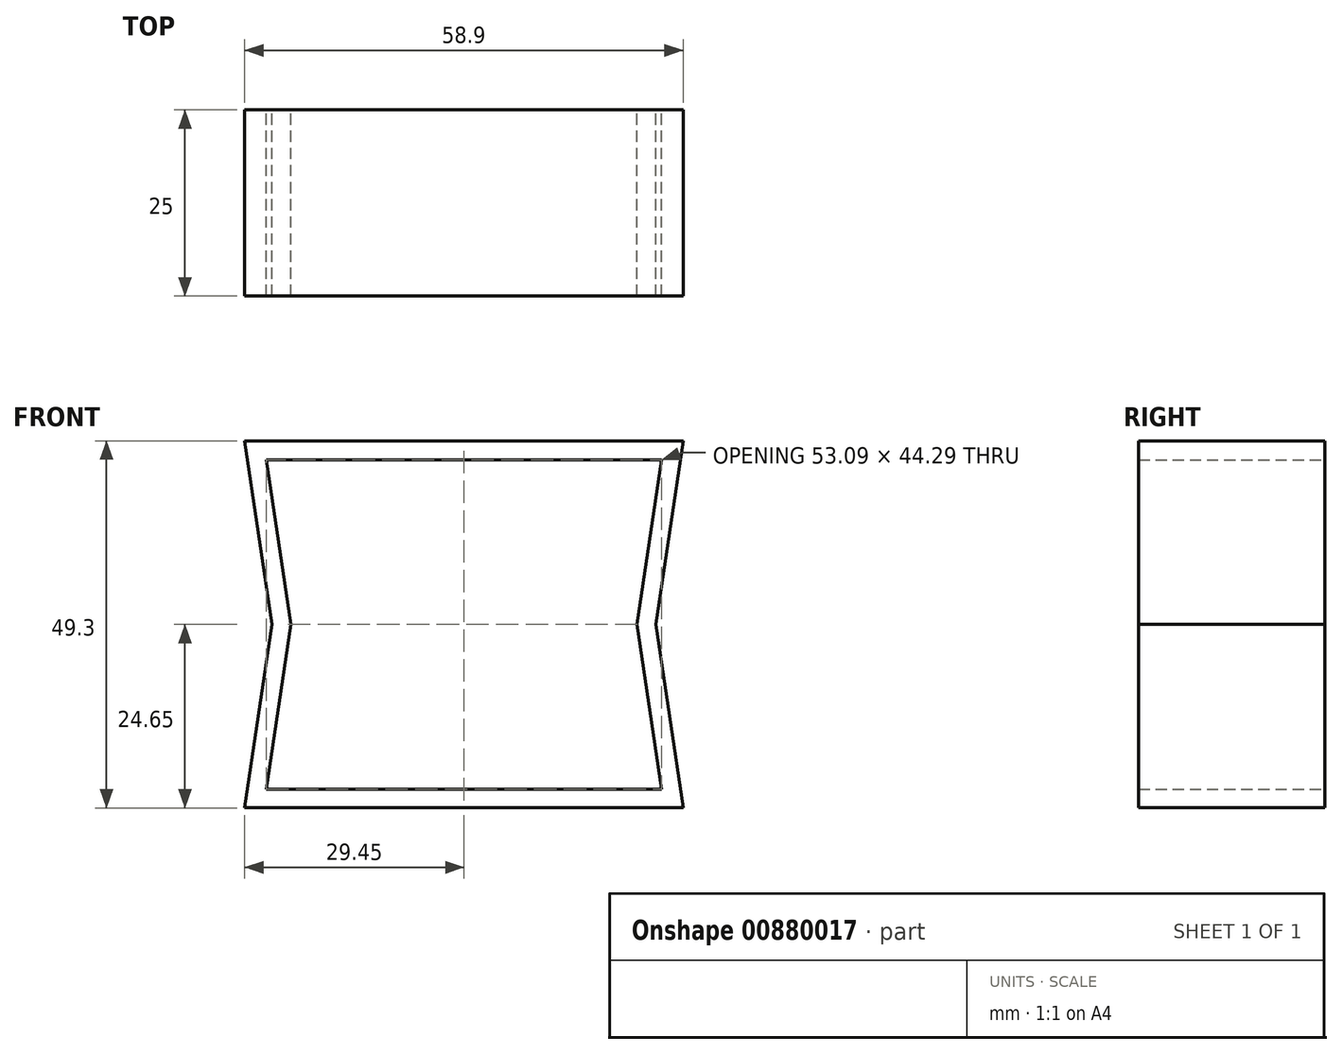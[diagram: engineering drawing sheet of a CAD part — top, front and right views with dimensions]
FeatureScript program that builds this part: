
annotation { "Feature Type Name" : "Feature", "Feature Type Description" : "" }
export const myFeature = defineFeature(function(context is Context, id is Id, definition is map)
    precondition{}
    {
        {
            var Q0;
            Q0=qCreatedBy(makeId("Front.planeOp"),FACE);
            var sketch = newSketch(context, id + "F0", { "sketchPlane" : qUnion([Q0])});
            skLineSegment(sketch, "E0", {"start": v(0, -24.65) * mm, "end": v(29.45, -24.65) * mm});
            skLineSegment(sketch, "E1", {"start": v(29.45, -24.65) * mm, "end": v(25.76, 0) * mm});
            skLineSegment(sketch, "E2.MirrorCS", {"start": v(-29.45, -24.65) * mm, "end": v(-25.76, 0) * mm});
            skLineSegment(sketch, "E3.MirrorCS", {"start": v(0, -24.65) * mm, "end": v(-29.45, -24.65) * mm});
            skLineSegment(sketch, "E4.MirrorCS", {"start": v(29.45, 24.65) * mm, "end": v(25.76, 0) * mm});
            skLineSegment(sketch, "E5.MirrorCS", {"start": v(0, 24.65) * mm, "end": v(29.45, 24.65) * mm});
            skLineSegment(sketch, "E6.MirrorCS", {"start": v(-29.45, 24.65) * mm, "end": v(-25.76, 0) * mm});
            skLineSegment(sketch, "E7.MirrorCS", {"start": v(0, 24.65) * mm, "end": v(-29.45, 24.65) * mm});
            skLineSegment(sketch, "E8.0", {"start": v(0, -22.15) * mm, "end": v(26.54, -22.15) * mm});
            skLineSegment(sketch, "E8.1", {"start": v(0, -22.15) * mm, "end": v(-26.54, -22.15) * mm});
            skLineSegment(sketch, "E8.2", {"start": v(26.54, -22.15) * mm, "end": v(23.23, 0) * mm});
            skLineSegment(sketch, "E8.3", {"start": v(-26.54, -22.15) * mm, "end": v(-23.23, 0) * mm});
            skLineSegment(sketch, "E8.4", {"start": v(26.54, 22.15) * mm, "end": v(23.23, 0) * mm});
            skLineSegment(sketch, "E8.5", {"start": v(0, 22.15) * mm, "end": v(26.54, 22.15) * mm});
            skLineSegment(sketch, "E8.6", {"start": v(0, 22.15) * mm, "end": v(-26.54, 22.15) * mm});
            skLineSegment(sketch, "E8.7", {"start": v(-26.54, 22.15) * mm, "end": v(-23.23, 0) * mm});
            skSolve(sketch);
        }
        {
            var Q0;
            Q0=makeQuery(id+"F0.imprint","IMPRINT",FACE,{"disambiguationData":[TD([[makeQuery(id+"F0.imprint","IMPRINT",EDGE,{"derivedFrom":sQuery(id+"F0.wireOp",EDGE,"E0")}),1.0]])]});
            extrude(context, id + "F1", {"entities" : qUnion([Q0]), "depth" : 25 * mm, "offsetDistance" : 25 * mm});
        }
    });
